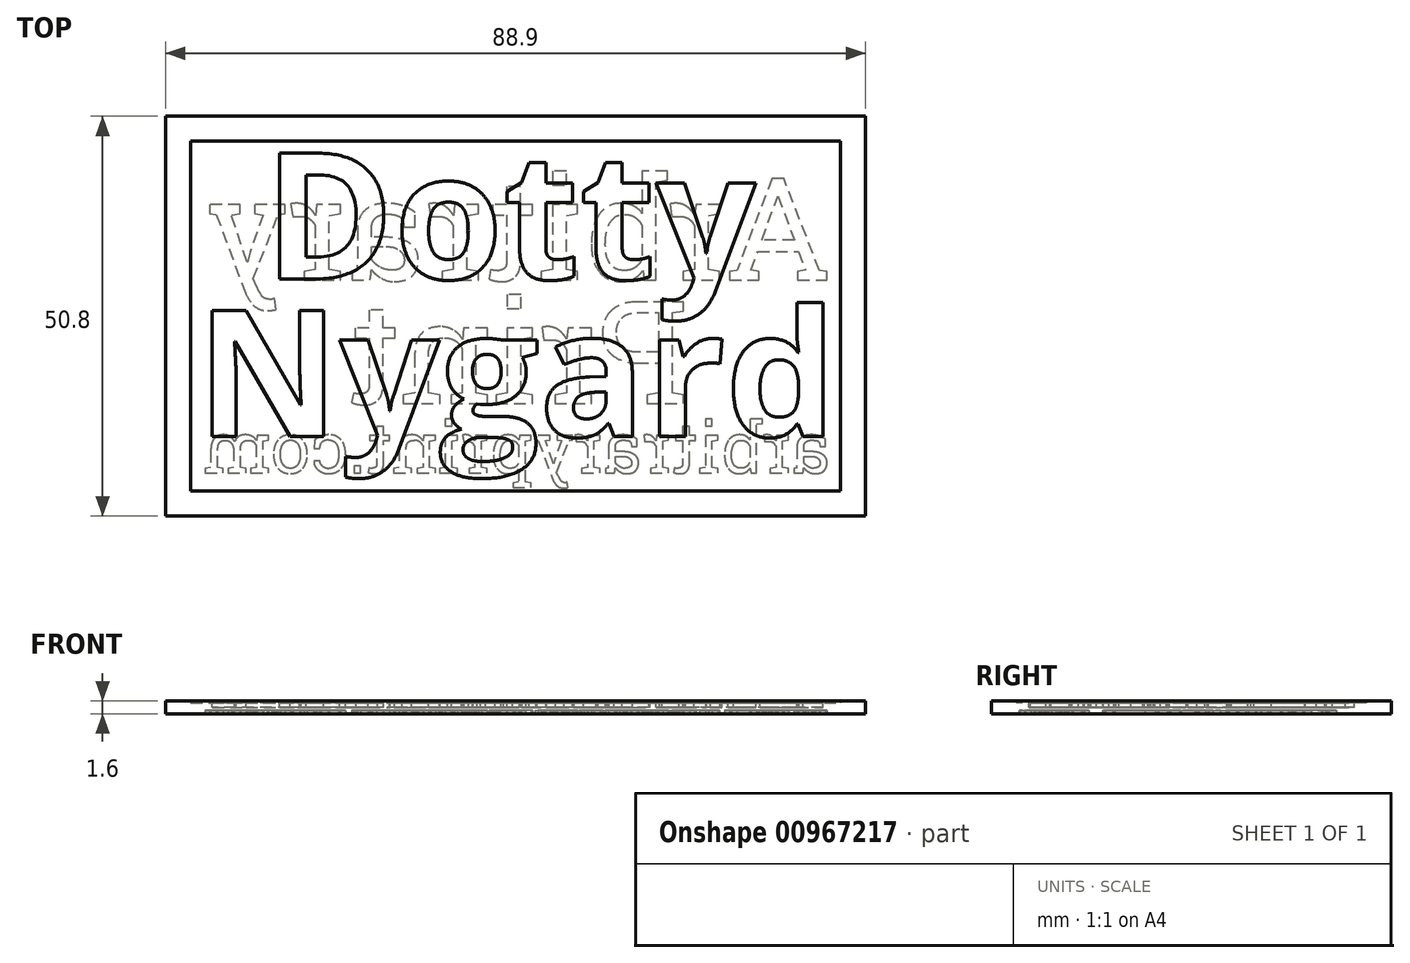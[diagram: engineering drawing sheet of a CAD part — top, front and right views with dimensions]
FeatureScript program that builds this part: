
annotation { "Feature Type Name" : "Feature", "Feature Type Description" : "" }
export const myFeature = defineFeature(function(context is Context, id is Id, definition is map)
    precondition{}
    {
        {
            assignVariable(context, id + "F0", {"name" : "cardThickness", "anyValue" : 1.4 * mm});
        }
        {
            assignVariable(context, id + "F1", {"name" : "engraveDepth", "anyValue" : .4});
        }
        {
            assignVariable(context, id + "F2", {"name" : "embossHeight", "anyValue" : .2});
        }
        {
            var Q0;
            Q0=qCreatedBy(makeId("Top.planeOp"),FACE);
            var sketch = newSketch(context, id + "F3", { "sketchPlane" : qUnion([Q0])});
            skLineSegment(sketch, "E0.bottom", {"start": v(-44.45, 25.4) * mm, "end": v(44.45, 25.4) * mm});
            skLineSegment(sketch, "E0.top", {"start": v(-44.45, -25.4) * mm, "end": v(44.45, -25.4) * mm});
            skLineSegment(sketch, "E0.left", {"start": v(-44.45, 25.4) * mm, "end": v(-44.45, -25.4) * mm});
            skLineSegment(sketch, "E0.right", {"start": v(44.45, 25.4) * mm, "end": v(44.45, -25.4) * mm});
            skPoint(sketch, "E0.middle", {"position": v(0, 0) * mm});
            skSolve(sketch);
        }
        {
            var Q0;
            Q0=qSketchRegion(id+"F3",true);
            extrude(context, id + "F4", {"entities" : qUnion([Q0]), "depth" : getVariable(context, 'cardThickness'), "offsetDistance" : 25.4 * mm, "symmetric" : true});
        }
        {
            var Q0;
            Q0=makeQuery(id+"F4.opExtrude","CAP_FACE",FACE,{"disambiguationData":[OSD([sQuery(id+"F3.wireOp",EDGE,"E0.bottom"),sQuery(id+"F3.wireOp",EDGE,"E0.top"),sQuery(id+"F3.wireOp",EDGE,"E0.left"),sQuery(id+"F3.wireOp",EDGE,"E0.right")])],"isStart":false});
            var sketch = newSketch(context, id + "F5", { "sketchPlane" : qUnion([Q0])});
            skLineSegment(sketch, "E1.bottom", {"start": v(-41.27, 22.22) * mm, "end": v(41.27, 22.23) * mm, "construction": true});
            skLineSegment(sketch, "E1.top", {"start": v(-41.27, -22.23) * mm, "end": v(41.27, -22.22) * mm, "construction": true});
            skLineSegment(sketch, "E1.left", {"start": v(-41.27, 22.22) * mm, "end": v(-41.27, -22.22) * mm, "construction": true});
            skLineSegment(sketch, "E1.right", {"start": v(41.27, 22.22) * mm, "end": v(41.27, -22.22) * mm, "construction": true});
            skPoint(sketch, "E1.middle", {"position": v(0, 0) * mm});
            skLineSegment(sketch, "E2", {"start": v(0, 22.22) * mm, "end": v(0, -22.22) * mm, "construction": true});
            skLineSegment(sketch, "E3", {"start": v(-41.27, 0) * mm, "end": v(41.27, 0) * mm, "construction": true});
            skLineSegment(sketch, "E4", {"start": v(0, 0) * mm, "end": v(0, 22.23) * mm, "construction": true});
            skLineSegment(sketch, "E5", {"start": v(0, 11.11) * mm, "end": v(-41.27, 11.11) * mm, "construction": true});
            skLineSegment(sketch, "E6", {"start": v(0, 0) * mm, "end": v(0, -22.22) * mm, "construction": true});
            skLineSegment(sketch, "E7", {"start": v(0, -11.11) * mm, "end": v(-41.27, -11.11) * mm, "construction": true});
            skLineSegment(sketch, "E8", {"start": v(0, 11.11) * mm, "end": v(0, 22.22) * mm, "construction": true});
            skLineSegment(sketch, "E9", {"start": v(0, 11.11) * mm, "end": v(0, 0) * mm, "construction": true});
            skLineSegment(sketch, "E10", {"start": v(0, 5.56) * mm, "end": v(41.27, 5.56) * mm, "construction": true});
            skLineSegment(sketch, "E11", {"start": v(0, 16.67) * mm, "end": v(41.27, 16.67) * mm, "construction": true});
            skLineSegment(sketch, "E12", {"start": v(0, -11.11) * mm, "end": v(0, 0) * mm, "construction": true});
            skLineSegment(sketch, "E13", {"start": v(0, -22.22) * mm, "end": v(0, -11.11) * mm, "construction": true});
            skLineSegment(sketch, "E14", {"start": v(0, -16.67) * mm, "end": v(41.27, -16.67) * mm, "construction": true});
            skLineSegment(sketch, "E15", {"start": v(0, -5.56) * mm, "end": v(41.27, -5.56) * mm, "construction": true});
            skLineSegment(sketch, "E16", {"start": v(0, -11.11) * mm, "end": v(41.27, -11.11) * mm, "construction": true});
            skLineSegment(sketch, "E17.MirrorCS", {"start": v(41.27, -22.23) * mm, "end": v(-41.27, -22.22) * mm, "construction": true});
            skLineSegment(sketch, "E18.MirrorCS", {"start": v(41.27, 22.22) * mm, "end": v(-41.27, 22.23) * mm, "construction": true});
            skLineSegment(sketch, "E19.MirrorCS", {"start": v(0, 11.11) * mm, "end": v(41.27, 11.11) * mm, "construction": true});
            skLineSegment(sketch, "E20.MirrorCS", {"start": v(0, -5.56) * mm, "end": v(-41.27, -5.56) * mm, "construction": true});
            skLineSegment(sketch, "E21.MirrorCS", {"start": v(0, -16.67) * mm, "end": v(-41.27, -16.67) * mm, "construction": true});
            skLineSegment(sketch, "E22.MirrorCS", {"start": v(41.27, 0) * mm, "end": v(-41.27, 0) * mm, "construction": true});
            skLineSegment(sketch, "E23.MirrorCS", {"start": v(0, 16.67) * mm, "end": v(-41.27, 16.67) * mm, "construction": true});
            skLineSegment(sketch, "E24.MirrorCS", {"start": v(0, 5.56) * mm, "end": v(-41.27, 5.56) * mm, "construction": true});
            skSolve(sketch);
        }
        {
            var Q0;
            Q0=makeQuery(id+"F5.imprint","IMPRINT",FACE,{"disambiguationData":[TD([[makeQuery(id+"F5.imprint","IMPRINT",EDGE,{"derivedFrom":makeQuery(id+"F4.opExtrude","CAP_EDGE",EDGE,{"disambiguationData":[OSD([sQuery(id+"F3.wireOp",EDGE,"E0.bottom")])],"isStart":false})}),-1.0]])]});
            var sketch = newSketch(context, id + "F6", { "sketchPlane" : qUnion([Q0])});
            skLineSegment(sketch, "E25.0", {"start": v(-41.27, 22.22) * mm, "end": v(41.27, 22.23) * mm, "construction": true});
            skLineSegment(sketch, "E26.0", {"start": v(41.27, 0) * mm, "end": v(-41.27, 0) * mm, "construction": true});
            skLineSegment(sketch, "E27.0", {"start": v(-41.27, -22.23) * mm, "end": v(41.27, -22.22) * mm, "construction": true});
            skText(sketch, "E28", { "text": "Dotty", "fontName": "OpenSans-Bold.ttf"});
            skText(sketch, "E29", { "text": "Nygard", "fontName": "OpenSans-Bold.ttf"});
            skLineSegment(sketch, "E30", {"start": v(-41.27, -7.23) * mm, "end": v(41.27, -7.22) * mm, "construction": true});
            skPoint(sketch, "E31", {"position": v(31.99, 12.78) * mm});
            skLineSegment(sketch, "E32", {"start": v(-31.99, 12.77) * mm, "end": v(31.99, 12.78) * mm, "construction": true});
            skPoint(sketch, "E33", {"position": v(0, 12.77) * mm});
            skPoint(sketch, "E34", {"position": v(40.53, -7.22) * mm});
            skPoint(sketch, "E35", {"position": v(-40.53, -7.23) * mm});
            const initialGuessF6  = {"E28": [-0.03199, 0.00473, 1, 0, 0.0161], "E29": [-0.04053, -0.01527, 1, 0, 0.0161]};
            skSetInitialGuess(sketch, initialGuessF6);
            skSolve(sketch);
        }
        {
            var Q0;
            Q0=makeQuery(id+"F5.imprint","IMPRINT",FACE,{"disambiguationData":[TD([[makeQuery(id+"F5.imprint","IMPRINT",EDGE,{"derivedFrom":makeQuery(id+"F4.opExtrude","CAP_EDGE",EDGE,{"disambiguationData":[OSD([sQuery(id+"F3.wireOp",EDGE,"E0.bottom")])],"isStart":false})}),-1.0]])]});
            var sketch = newSketch(context, id + "F7", { "sketchPlane" : qUnion([Q0])});
            skLineSegment(sketch, "E36.bottom", {"start": v(-41.27, 22.22) * mm, "end": v(41.27, 22.22) * mm});
            skLineSegment(sketch, "E36.top", {"start": v(-41.27, -22.22) * mm, "end": v(41.27, -22.22) * mm});
            skLineSegment(sketch, "E36.left", {"start": v(-41.27, 22.22) * mm, "end": v(-41.27, -22.22) * mm});
            skLineSegment(sketch, "E36.right", {"start": v(41.27, 22.22) * mm, "end": v(41.27, -22.22) * mm});
            skPoint(sketch, "E36.middle", {"position": v(0, 0) * mm});
            skLineSegment(sketch, "E37.bottom", {"start": v(-44.45, 25.4) * mm, "end": v(44.45, 25.4) * mm});
            skLineSegment(sketch, "E37.top", {"start": v(-44.45, -25.4) * mm, "end": v(44.45, -25.4) * mm});
            skLineSegment(sketch, "E37.left", {"start": v(-44.45, 25.4) * mm, "end": v(-44.45, -25.4) * mm});
            skLineSegment(sketch, "E37.right", {"start": v(44.45, 25.4) * mm, "end": v(44.45, -25.4) * mm});
            skSolve(sketch);
        }
        {
            var Q0;
            Q0=qSketchRegion(id+"F7",true);
            extrude(context, id + "F8", {"entities" : qUnion([Q0]), "operationType" : NewBodyOperationType.ADD, "depth" : (getVariable(context, 'embossHeight')) * mm, "offsetDistance" : 25 * mm});
        }
        {
            var Q0;
            Q0=makeQuery(id+"F4.opExtrude","CAP_FACE",FACE,{"disambiguationData":[OSD([sQuery(id+"F3.wireOp",EDGE,"E0.bottom"),sQuery(id+"F3.wireOp",EDGE,"E0.top"),sQuery(id+"F3.wireOp",EDGE,"E0.left"),sQuery(id+"F3.wireOp",EDGE,"E0.right")])],"isStart":true});
            var sketch = newSketch(context, id + "F9", { "sketchPlane" : qUnion([Q0])});
            skLineSegment(sketch, "E38.0", {"start": v(0, 11.11) * mm, "end": v(-41.27, 11.11) * mm, "construction": true});
            skLineSegment(sketch, "E38.1", {"start": v(0, -16.67) * mm, "end": v(-41.27, -16.67) * mm, "construction": true});
            skText(sketch, "E39", { "text": "arbitraryprint.com", "fontName": "RobotoSlab-Regular.ttf"});
            skText(sketch, "E40", { "text": "Arbitrary", "fontName": "RobotoSlab-Regular.ttf"});
            skText(sketch, "E41", { "text": "Print", "fontName": "RobotoSlab-Regular.ttf"});
            skLineSegment(sketch, "E42.0", {"start": v(-41.27, -22.23) * mm, "end": v(41.27, -22.22) * mm, "construction": true});
            skLineSegment(sketch, "E43.0", {"start": v(41.27, 22.23) * mm, "end": v(-41.28, 22.22) * mm, "construction": true});
            skLineSegment(sketch, "E44.0", {"start": v(41.27, 22.23) * mm, "end": v(41.28, -22.22) * mm, "construction": true});
            skLineSegment(sketch, "E44.1", {"start": v(-41.27, 22.23) * mm, "end": v(-41.27, -22.22) * mm, "construction": true});
            const initialGuessF9  = {"E39": [0.04002, 0.01992, -1, 0, 0.0065], "E40": [0.04003, -0.00457, -1, 0, 0.01308], "E41": [0.02198, 0.01111, -1, 0, 0.01308]};
            skSetInitialGuess(sketch, initialGuessF9);
            skSolve(sketch);
        }
        {
            var Q0;
            Q0=qSketchRegion(id+"F9",true);
            extrude(context, id + "F10", {"entities" : qUnion([Q0]), "operationType" : NewBodyOperationType.REMOVE, "oppositeDirection" : true, "depth" : (getVariable(context, 'engraveDepth')) * mm, "offsetDistance" : 25 * mm});
        }
        {
            var Q0;
            Q0 = qSketchRegion(id + "F6", true);
            extrude(context, id + "F11", {"entities" : qUnion([Q0]), "operationType" : NewBodyOperationType.REMOVE, "oppositeDirection" : true, "depth" : .6 * mm, "offsetDistance" : 25 * mm});
        }
    });
